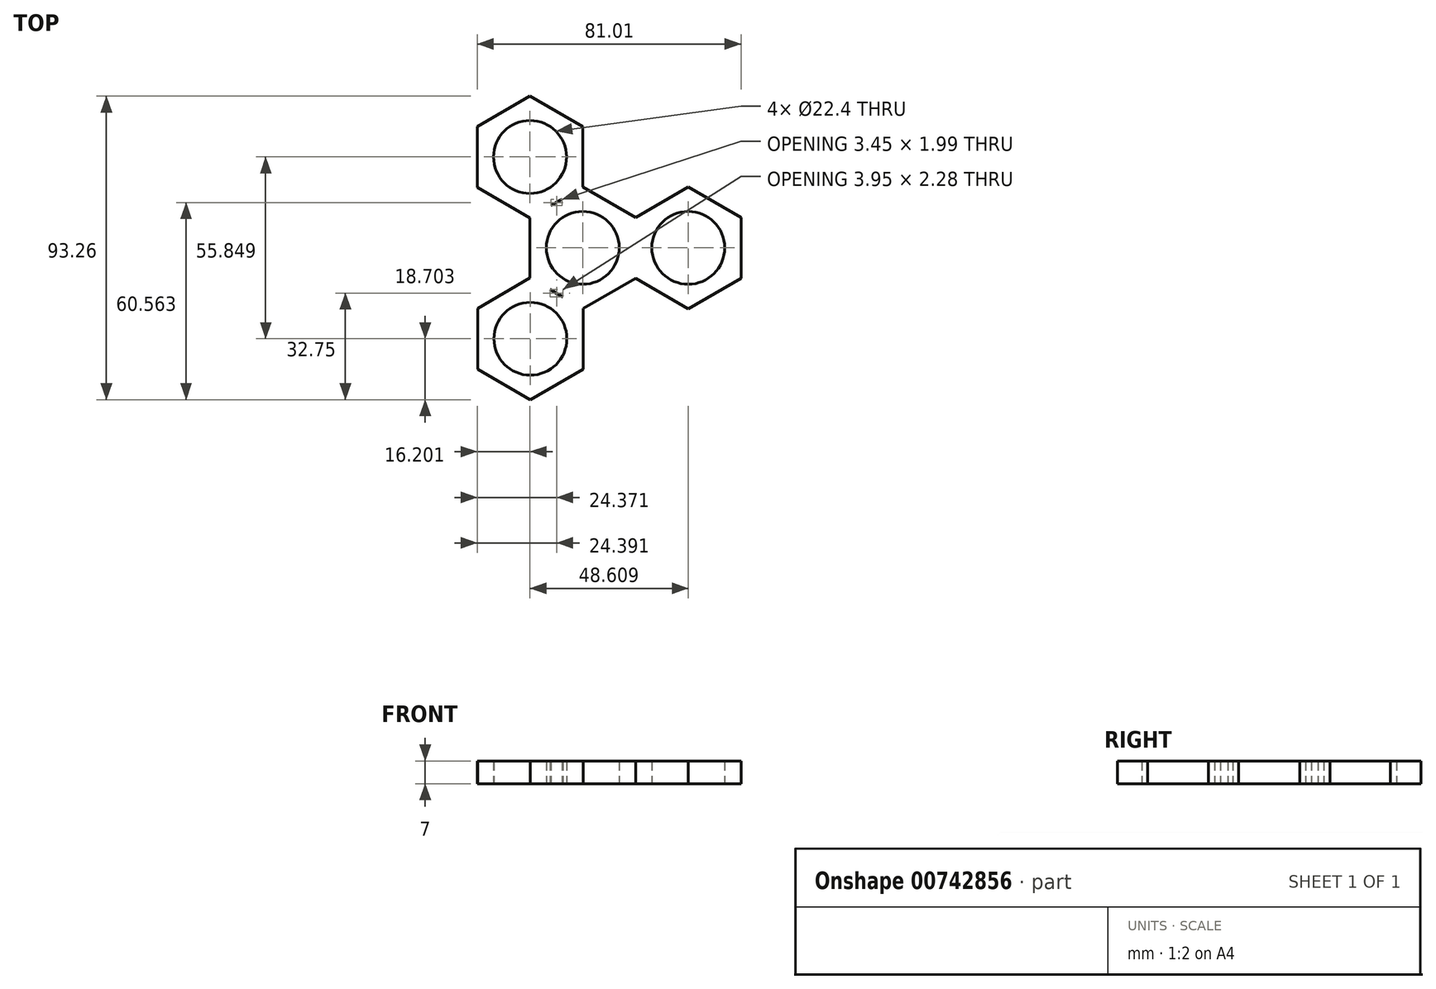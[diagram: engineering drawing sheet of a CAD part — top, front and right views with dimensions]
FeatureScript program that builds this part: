
annotation { "Feature Type Name" : "Feature", "Feature Type Description" : "" }
export const myFeature = defineFeature(function(context is Context, id is Id, definition is map)
    precondition{}
    {
        {
            var Q0;
            Q0=qCreatedBy(makeId("Top.planeOp"),FACE);
            var sketch = newSketch(context, id + "F0", { "sketchPlane" : qUnion([Q0])});
            skCircle(sketch, "E0", {"center": v(0, 0) * mm, "radius": 16.2 * mm});
            skCircle(sketch, "E1", {"center": v(0, 0) * mm, "radius": 11.2 * mm});
            skCircle(sketch, "E2.cCircle", {"center": v(0, 0) * mm, "radius": 16.2 * mm, "construction": true});
            skLineSegment(sketch, "E2.0", {"start": v(-16.2, -9.35) * mm, "end": v(-16.2, 9.35) * mm});
            skLineSegment(sketch, "E2.1", {"start": v(-16.2, 9.35) * mm, "end": v(0, 18.7) * mm});
            skLineSegment(sketch, "E2.2", {"start": v(0, 18.7) * mm, "end": v(16.2, 9.35) * mm});
            skLineSegment(sketch, "E2.3", {"start": v(16.2, 9.35) * mm, "end": v(16.2, -9.35) * mm});
            skLineSegment(sketch, "E2.4", {"start": v(16.2, -9.35) * mm, "end": v(0, -18.7) * mm});
            skLineSegment(sketch, "E2.5", {"start": v(0, -18.7) * mm, "end": v(-16.2, -9.35) * mm});
            skPoint(sketch, "E2.0.midPoint", {"position": v(-16.2, 0) * mm});
            skCircle(sketch, "E3", {"center": v(32.4, 0) * mm, "radius": 11.2 * mm});
            skLineSegment(sketch, "E4.0", {"start": v(16.2, -9.35) * mm, "end": v(16.2, 9.35) * mm});
            skLineSegment(sketch, "E4.1", {"start": v(16.2, 9.35) * mm, "end": v(32.4, 18.7) * mm});
            skLineSegment(sketch, "E4.2", {"start": v(32.4, 18.7) * mm, "end": v(48.6, 9.35) * mm});
            skLineSegment(sketch, "E4.3", {"start": v(48.6, 9.35) * mm, "end": v(48.6, -9.35) * mm});
            skLineSegment(sketch, "E4.4", {"start": v(48.6, -9.35) * mm, "end": v(32.4, -18.7) * mm});
            skLineSegment(sketch, "E4.5", {"start": v(32.4, -18.7) * mm, "end": v(16.2, -9.35) * mm});
            skCircle(sketch, "E5", {"center": v(-16.2, 27.91) * mm, "radius": 11.2 * mm});
            skLineSegment(sketch, "E6.0", {"start": v(-32.4, 18.56) * mm, "end": v(-32.4, 37.27) * mm});
            skLineSegment(sketch, "E6.1", {"start": v(-32.4, 37.27) * mm, "end": v(-16.2, 46.62) * mm});
            skLineSegment(sketch, "E6.2", {"start": v(-16.2, 46.62) * mm, "end": v(0, 37.27) * mm});
            skLineSegment(sketch, "E6.3", {"start": v(0, 37.27) * mm, "end": v(0, 18.56) * mm});
            skLineSegment(sketch, "E6.4", {"start": v(0, 18.56) * mm, "end": v(-16.2, 9.2) * mm});
            skLineSegment(sketch, "E6.5", {"start": v(-16.2, 9.2) * mm, "end": v(-32.4, 18.56) * mm});
            skCircle(sketch, "E7", {"center": v(-16.09, -27.94) * mm, "radius": 11.2 * mm});
            skLineSegment(sketch, "E8.0", {"start": v(-32.29, -37.3) * mm, "end": v(-32.29, -18.58) * mm});
            skLineSegment(sketch, "E8.1", {"start": v(-32.29, -18.58) * mm, "end": v(-16.09, -9.23) * mm});
            skLineSegment(sketch, "E8.2", {"start": v(-16.09, -9.23) * mm, "end": v(0.11, -18.58) * mm});
            skLineSegment(sketch, "E8.3", {"start": v(0.11, -18.58) * mm, "end": v(0.11, -37.3) * mm});
            skLineSegment(sketch, "E8.4", {"start": v(0.11, -37.3) * mm, "end": v(-16.09, -46.64) * mm});
            skLineSegment(sketch, "E8.5", {"start": v(-16.09, -46.64) * mm, "end": v(-32.29, -37.3) * mm});
            skSolve(sketch);
        }
        {
            var Q0;
            Q0 = qSketchRegion(id + "F0", true);
            var Q1;
            {var subQ0=sQuery(id+"F0.wireOp",EDGE,"E8.2");var subQ1=sQuery(id+"F0.wireOp",EDGE,"E0");var subQ2=makeQuery(id+"F0.imprint","INTERSECT",VERTEX,{"disambiguationData":[OD(0.0)],"derivedFrom":[subQ1,subQ0]});Q1=makeQuery(id+"F0.imprint","IMPRINT",FACE,{"disambiguationData":[TD([[makeQuery(id+"F0.imprint","IMPRINT",EDGE,{"disambiguationData":[TD([[subQ2,-1.0]])],"derivedFrom":subQ1}),1.0]])]});}
            var Q2;
            {var subQ0=sQuery(id+"F0.wireOp",EDGE,"E6.4");var subQ1=sQuery(id+"F0.wireOp",EDGE,"E0");var subQ2=makeQuery(id+"F0.imprint","INTERSECT",VERTEX,{"disambiguationData":[OD(0.0)],"derivedFrom":[subQ1,subQ0]});Q2=makeQuery(id+"F0.imprint","IMPRINT",FACE,{"disambiguationData":[TD([[makeQuery(id+"F0.imprint","IMPRINT",EDGE,{"disambiguationData":[TD([[subQ2,-1.0]])],"derivedFrom":subQ1}),1.0]])]});}
            extrude(context, id + "F1", {"entities" : qUnion([Q0, Q1, Q2]), "depth" : 7 * mm, "offsetDistance" : 25.4 * mm});
        }
    });
